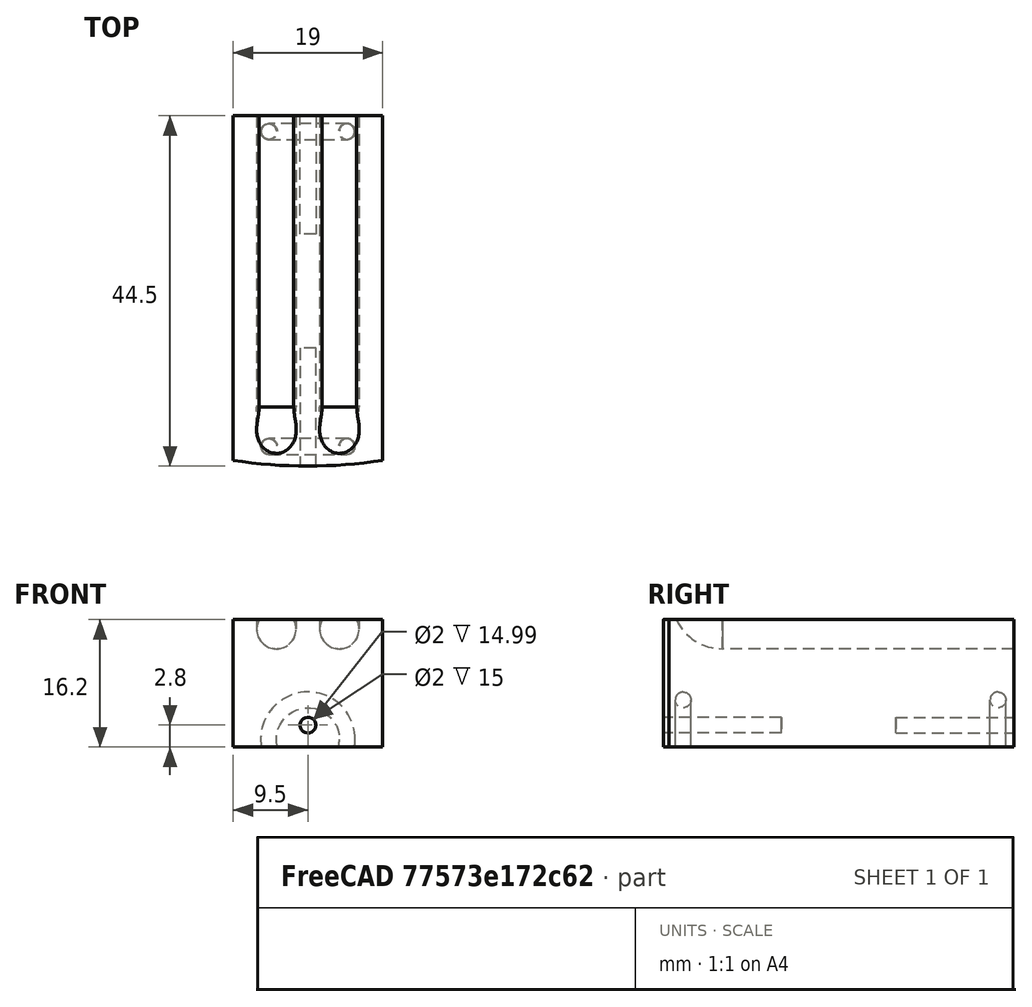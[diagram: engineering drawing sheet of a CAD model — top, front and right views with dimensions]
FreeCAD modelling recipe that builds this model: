
FCSTD DOCUMENT  (FreeCAD 0.18R4 (GitTag))
Label: Ständer_für_Lampenfassung
License: All rights reserved
LicenseURL: http://en.wikipedia.org/wiki/All_rights_reserved
objects: Sketcher::SketchObject×4, Part::Cut×4, PartDesign::Pocket×2, PartDesign::Body×2, Part::Torus×2, Part::Cylinder×2, Part::Fuse×2, Part::Mirroring×2, PartDesign::Pad×1, PartDesign::Revolution×1, App::Part×1, Mesh::Feature×1
note: 26 computed .brp shape members not serialized (recipe doc carries the construction recipe); baked Part::Feature solids carry a one-line shape summary decoded from their .brp

FEATURE [Sketcher::SketchObject] Sketch
  MapMode = 5
  Support = -> [XY_Plane001]
  sketch-geometry (5):
    g0: Circle [constr] CenterX=0 CenterY=0 CenterZ=0 NormalX=0 NormalY=0 NormalZ=1 AngleXU=0 Radius=62.5
    g1: LineSegment StartX=-9.5 StartY=-61.7738 StartZ=0 EndX=-9.5 EndY=-18 EndZ=0
    g2: LineSegment StartX=-9.5 StartY=-18 StartZ=0 EndX=9.5 EndY=-18 EndZ=0
    g3: LineSegment StartX=9.5 StartY=-18 StartZ=0 EndX=9.5 EndY=-61.7738 EndZ=0
    g4: ArcOfCircle CenterX=0 CenterY=0 CenterZ=0 NormalX=0 NormalY=0 NormalZ=1 AngleXU=0 Radius=62.5 StartAngle=4.5598 EndAngle=4.86498
  constraints (14):
    c: Radius(g0) = 62.5
    c: Coincident(g1,g2)
    c: Coincident(g2,g3)
    c: Parallel(g1,g3)
    c: Perpendicular(g2,g1)
    c: DistanceX(g2,g2) = 19
    c: DistanceY(g1,g-1) = 18
    c: DistanceX(g1,g-1) = 9.5
    c: Coincident(g4,g1)
    c: Coincident(g3,g4)
    c: Radius(g4) = 62.5
    c: Coincident(g4,g-1)
    c: Vertical(g1)
    c: Coincident(g4,g0)
FEATURE [PartDesign::Pad] Pad
  Length = 16.2
  Length2 = 100
  Profile = -> Sketch
  Type = 0
FEATURE [Sketcher::SketchObject] Sketch002
  AttachmentOffset = pos=(0,0,18) rot=(0,0,1;0rad)
  MapMode = 5
  Placement = pos=(0,-18,-4e-15) rot=(1,0,0;1.5708rad)
  Support = -> [XZ_Plane001]
  sketch-geometry (1):
    g0: Circle CenterX=0 CenterY=2.8 CenterZ=0 NormalX=0 NormalY=0 NormalZ=1 AngleXU=0 Radius=1
  constraints (3):
    c: DistanceY(g-1,g0) = 2.8
    c: Diameter(g0) = 2
    c: DistanceX(g0,g-1) = 0
FEATURE [PartDesign::Pocket] Pocket
  BaseFeature = -> Pad
  Length = 15
  Length2 = 100
  Profile = -> Sketch002
  Reversed = true
  Type = 0
FEATURE [Sketcher::SketchObject] Sketch003
  AttachmentOffset = pos=(0,0,62.51) rot=(0,0,1;0rad)
  MapMode = 5
  Placement = pos=(0,-62.51,-1.39e-14) rot=(1,0,0;1.5708rad)
  Support = -> [XZ_Plane001]
  sketch-geometry (1):
    g0: Circle CenterX=0 CenterY=2.8 CenterZ=0 NormalX=0 NormalY=0 NormalZ=1 AngleXU=0 Radius=1
  constraints (3):
    c: DistanceY(g-1,g0) = 2.8
    c: Diameter(g0) = 2
    c: DistanceX(g0,g-1) = 0
FEATURE [PartDesign::Pocket] Pocket001
  BaseFeature = -> Pocket
  Length = 15
  Length2 = 100
  Profile = -> Sketch003
  Type = 0
FEATURE [PartDesign::Body] Body
  Group = -> [Sketch,Pad,Sketch002,Pocket,Sketch003,Pocket001]
  Origin = -> Origin001
  Tip = -> Pocket001
FEATURE [Part::Torus] Torus
  Angle1 = -180
  Angle2 = 180
  Angle3 = 360
  AttacherType = Attacher::AttachEngine3D
  Placement = pos=(0,-60,1) rot=(1,0,0;1.5708rad)
  Radius1 = 5
  Radius2 = 1
FEATURE [Part::Torus] Torus001
  Angle1 = -180
  Angle2 = 180
  Angle3 = 360
  AttacherType = Attacher::AttachEngine3D
  Placement = pos=(0,-20,1) rot=(1,0,0;1.5708rad)
  Radius1 = 5
  Radius2 = 1
FEATURE [Part::Cylinder] Cylinder  label="Zylinder"
  Angle = 360
  AttacherType = Attacher::AttachEngine3D
  Height = 70
  Placement = pos=(4,-84,14) rot=(-1,0,0;1.5708rad)
  Radius = 2.5
FEATURE [Part::Cylinder] Cylinder001  label="Zylinder001"
  Angle = 360
  AttacherType = Attacher::AttachEngine3D
  Height = 10
  Placement = pos=(4,-10,18) rot=(0,0,1;0rad)
  Radius = 2.5
FEATURE [Sketcher::SketchObject] Sketch005
  MapMode = 5
  Placement = pos=(0,0,0) rot=(1,0,0;1.5708rad)
  Support = -> [XZ_Plane002]
  sketch-geometry (1):
    g0: Circle CenterX=4 CenterY=14 CenterZ=0 NormalX=0 NormalY=0 NormalZ=1 AngleXU=0 Radius=2.51
  constraints (3):
    c: Diameter(g0) = 5.02
    c: DistanceY(g-1,g0) = 14
    c: DistanceX(g-1,g0) = 4
FEATURE [PartDesign::Revolution] Revolution
  Angle = 90
  Axis = (0,2e-16,1)
  Base = (0,0,0)
  Placement = pos=(0,0,0) rot=(1,0,0;1.5708rad)
  Profile = -> Sketch005
  ReferenceAxis = -> Sketch005 [V_Axis]
  Reversed = true
FEATURE [PartDesign::Body] Body001
  Group = -> [Sketch005,Revolution]
  Origin = -> Origin002
  Placement = pos=(-10,-14,18) rot=(0.57735,0.57735,0.57735;2.0944rad)
  Tip = -> Revolution
FEATURE [App::Part] Part
  Group = -> [Body,Body001,Torus,Torus001]
  Origin = -> Origin
FEATURE [Part::Fuse] Fusion
  Base = -> Body001
  Tool = -> Cylinder
FEATURE [Part::Fuse] Fusion001
  Base = -> Cylinder001
  Tool = -> Fusion
FEATURE [Part::Mirroring] Part__Mirroring  label="Fusion001 (Mirror #1)"
  Base = (0,0,0)
  Normal = (0,1,0)
  Placement = pos=(0,-69,1) rot=(0,0,1;0rad)
  Source = -> Fusion001
FEATURE [Part::Mirroring] Part__Mirroring001  label="Fusion001 (Mirror #1)001"
  Base = (0,0,0)
  Normal = (0,1,0)
  Placement = pos=(-8,-69,1) rot=(0,0,1;0rad)
  Source = -> Fusion001
FEATURE [Part::Cut] Cut
  Base = -> Body
  Tool = -> Part__Mirroring
FEATURE [Part::Cut] Cut001
  Base = -> Cut
  Tool = -> Part__Mirroring001
FEATURE [Part::Cut] Cut002
  Base = -> Cut001
  Tool = -> Torus
FEATURE [Part::Cut] Cut003  label="Cut003 Alles"
  Base = -> Cut002
  Tool = -> Torus001
FEATURE [Mesh::Feature] Mesh  label="Cut003 Alles (Meshed)"
